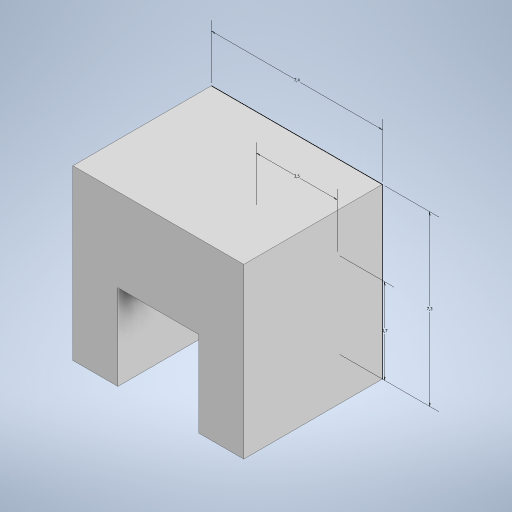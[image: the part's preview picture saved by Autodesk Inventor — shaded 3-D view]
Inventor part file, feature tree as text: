
AUTODESK INVENTOR PART (.ipt)
format: ipt  version: 2024.3 (Build 283343000, 343)  size: 247,808 bytes
history: native  units: mm
features: extrude x2, sketch x1
ambient origin geometry x8: Origin, YZ Plane, XZ Plane, XY Plane, X Axis, Y Axis, Z Axis, Center Point
bodies: Solid1 (feature_tree)
feature tree (3):
  sketch  "Sketch1"  dims[d0=7.4mm d1=7.3mm d2=3.5mm d3=3.7mm d4=6.0mm d5=0.0mm d6=2.0mm d7=0.0mm]
  extrude  "Extrusion1"  Depth=7.3mm
  extrude  "Extrusion2"  Depth=3.5mm
